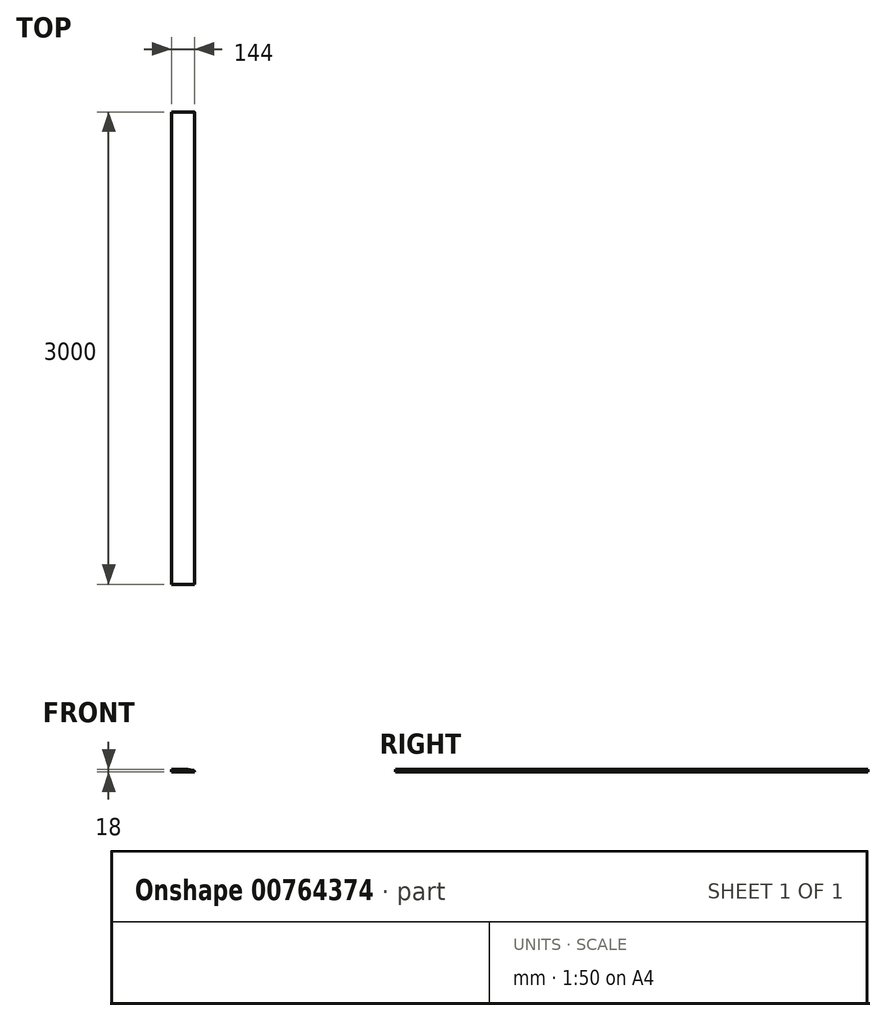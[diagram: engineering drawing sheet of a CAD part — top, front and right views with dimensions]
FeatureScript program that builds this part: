
annotation { "Feature Type Name" : "Feature", "Feature Type Description" : "" }
export const myFeature = defineFeature(function(context is Context, id is Id, definition is map)
    precondition{}
    {
        {
            var Q0;
            Q0=qCreatedBy(makeId("Front.planeOp"),FACE);
            var sketch = newSketch(context, id + "F0", { "sketchPlane" : qUnion([Q0])});
            skLineSegment(sketch, "E0", {"start": v(-44.12, 0) * mm, "end": v(-44.12, 18) * mm});
            skLineSegment(sketch, "E1", {"start": v(99.88, 0) * mm, "end": v(-44.12, 0) * mm});
            skLineSegment(sketch, "E2", {"start": v(-44.12, 18) * mm, "end": v(54.98, 18) * mm});
            skLineSegment(sketch, "E3", {"start": v(99.88, 0) * mm, "end": v(99.88, 1.65) * mm});
            skLineSegment(sketch, "E4", {"start": v(91.66, 11.5) * mm, "end": v(56.77, 17.84) * mm});
            skPoint(sketch, "E5.visualSharp", {"position": v(55.88, 18) * mm});
            skArc(sketch, "E5.filletArc", {"start": v(56.77, 17.84) * mm, "mid": v(55.88, 17.96) * mm, "end": v(54.98, 18) * mm});
            skPoint(sketch, "E6.visualSharp", {"position": v(99.88, 10) * mm});
            skArc(sketch, "E6.filletArc", {"start": v(99.88, 1.65) * mm, "mid": v(97.55, 8.06) * mm, "end": v(91.66, 11.5) * mm});
            skSolve(sketch);
        }
        {
            var Q0;
            Q0=makeQuery(id+"F0.imprint","IMPRINT",FACE,{"disambiguationData":[TD([[makeQuery(id+"F0.imprint","IMPRINT",EDGE,{"derivedFrom":sQuery(id+"F0.wireOp",EDGE,"E0")}),-1.0]])]});
            extrude(context, id + "F1", {"entities" : qUnion([Q0]), "depth" : 3000 * mm, "offsetDistance" : 25 * mm, "symmetric" : true});
        }
    });
